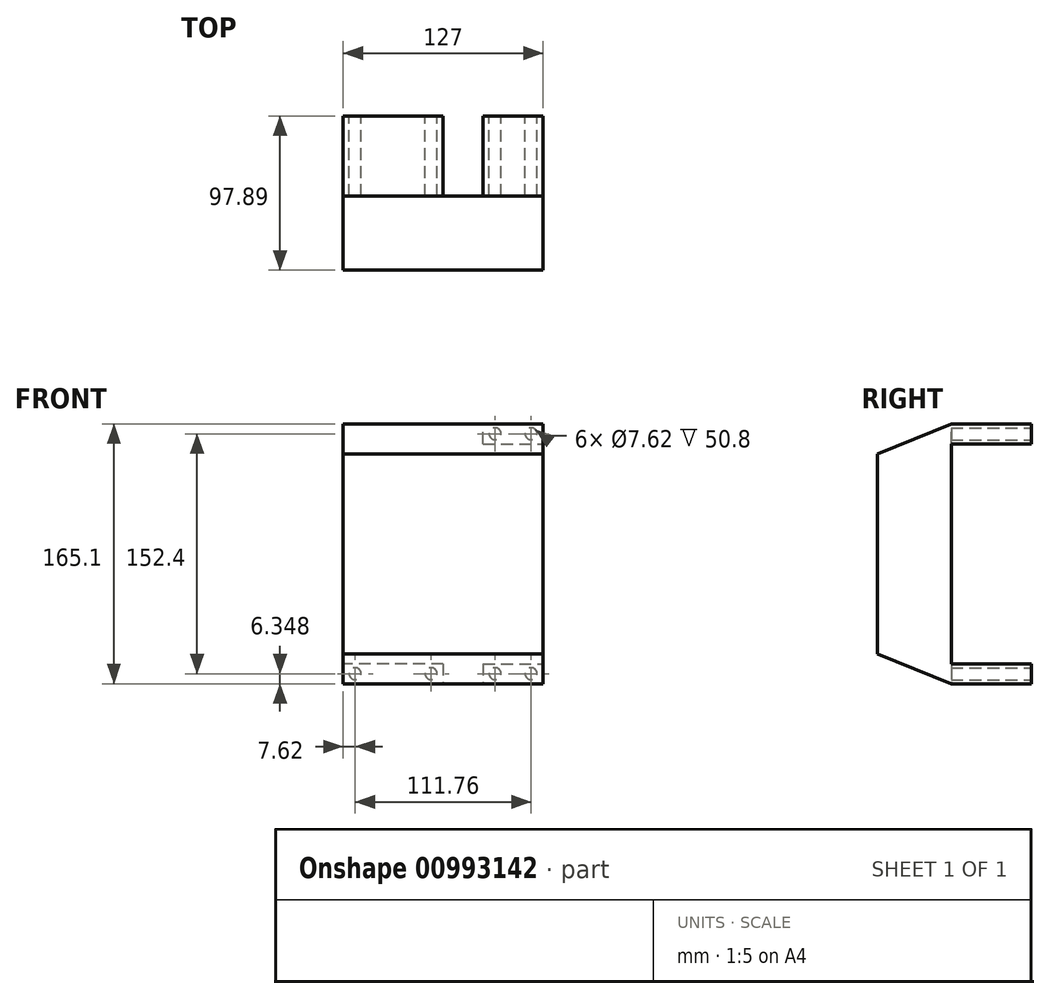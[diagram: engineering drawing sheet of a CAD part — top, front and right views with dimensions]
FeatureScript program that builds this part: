
annotation { "Feature Type Name" : "Feature", "Feature Type Description" : "" }
export const myFeature = defineFeature(function(context is Context, id is Id, definition is map)
    precondition{}
    {
        {
            var Q0;
            Q0=qCreatedBy(makeId("Right.planeOp"),FACE);
            var sketch = newSketch(context, id + "F0", { "sketchPlane" : qUnion([Q0])});
            skLineSegment(sketch, "E0", {"start": v(37.9, 107.88) * mm, "end": v(37.9, -57.22) * mm});
            skLineSegment(sketch, "E1", {"start": v(37.9, 107.88) * mm, "end": v(-9.2, 88.83) * mm});
            skLineSegment(sketch, "E2", {"start": v(-9.2, 88.83) * mm, "end": v(-9.2, -38.17) * mm});
            skLineSegment(sketch, "E3", {"start": v(-9.2, -38.17) * mm, "end": v(37.9, -57.22) * mm});
            skLineSegment(sketch, "E4.bottom", {"start": v(37.9, -57.22) * mm, "end": v(88.7, -57.22) * mm});
            skLineSegment(sketch, "E4.top", {"start": v(37.9, -44.52) * mm, "end": v(88.7, -44.52) * mm});
            skLineSegment(sketch, "E4.left", {"start": v(37.9, -57.22) * mm, "end": v(37.9, -44.52) * mm});
            skLineSegment(sketch, "E4.right", {"start": v(88.7, -57.22) * mm, "end": v(88.7, -44.52) * mm});
            skSolve(sketch);
        }
        {
            var Q0;
            Q0=makeQuery(id+"F0.imprint","IMPRINT",FACE,{"disambiguationData":[TD([[makeQuery(id+"F0.imprint","IMPRINT",EDGE,{"derivedFrom":sQuery(id+"F0.wireOp",EDGE,"E0")}),-1.0]])]});
            extrude(context, id + "F1", {"entities" : qUnion([Q0]), "depth" : 127 * mm, "offsetDistance" : 25.4 * mm});
        }
        {
            var Q0;
            Q0=makeQuery(id+"F0.imprint","IMPRINT",FACE,{"disambiguationData":[TD([[makeQuery(id+"F0.imprint","IMPRINT",EDGE,{"derivedFrom":sQuery(id+"F0.wireOp",EDGE,"E4.bottom")}),1.0]])]});
            extrude(context, id + "F2", {"entities" : qUnion([Q0]), "operationType" : NewBodyOperationType.ADD, "depth" : 63.5 * mm, "offsetDistance" : 25.4 * mm});
        }
        {
            var Q0;
            Q0=makeQuery(id+"F1.opExtrude","SWEPT_FACE",FACE,{"disambiguationData":[OSD([sQuery(id+"F0.wireOp",EDGE,"E0"),sQuery(id+"F0.wireOp",EDGE,"E4.left")])]});
            var sketch = newSketch(context, id + "F3", { "sketchPlane" : qUnion([Q0])});
            skLineSegment(sketch, "E5.bottom", {"start": v(-88.9, -44.52) * mm, "end": v(-127, -44.52) * mm});
            skLineSegment(sketch, "E5.top", {"start": v(-88.9, -57.22) * mm, "end": v(-127, -57.22) * mm});
            skLineSegment(sketch, "E5.left", {"start": v(-88.9, -44.52) * mm, "end": v(-88.9, -57.22) * mm});
            skLineSegment(sketch, "E5.right", {"start": v(-127, -44.52) * mm, "end": v(-127, -57.22) * mm});
            skLineSegment(sketch, "E6.bottom", {"start": v(-88.9, 95.18) * mm, "end": v(-127, 95.18) * mm});
            skLineSegment(sketch, "E6.top", {"start": v(-88.9, 107.88) * mm, "end": v(-127, 107.88) * mm});
            skLineSegment(sketch, "E6.left", {"start": v(-88.9, 95.18) * mm, "end": v(-88.9, 107.88) * mm});
            skLineSegment(sketch, "E6.right", {"start": v(-127, 95.18) * mm, "end": v(-127, 107.88) * mm});
            skSolve(sketch);
        }
        {
            var Q0;
            Q0=makeQuery(id+"F3.imprint","IMPRINT",FACE,{"disambiguationData":[TD([[makeQuery(id+"F3.imprint","IMPRINT",EDGE,{"derivedFrom":sQuery(id+"F3.wireOp",EDGE,"E5.bottom")}),1.0]])]});
            var Q1;
            Q1=makeQuery(id+"F3.imprint","IMPRINT",FACE,{"disambiguationData":[TD([[makeQuery(id+"F3.imprint","IMPRINT",EDGE,{"derivedFrom":sQuery(id+"F3.wireOp",EDGE,"E6.bottom")}),-1.0]])]});
            extrude(context, id + "F4", {"entities" : qUnion([Q0, Q1]), "operationType" : NewBodyOperationType.ADD, "depth" : 50.8 * mm, "offsetDistance" : 25.4 * mm});
        }
        {
            var Q0;
            Q0=makeQuery(id+"F4.opExtrude","CAP_FACE",FACE,{"disambiguationData":[OSD([sQuery(id+"F3.wireOp",EDGE,"E6.bottom"),sQuery(id+"F3.wireOp",EDGE,"E6.top"),sQuery(id+"F3.wireOp",EDGE,"E6.left"),sQuery(id+"F3.wireOp",EDGE,"E6.right")])],"isStart":false});
            var sketch = newSketch(context, id + "F5", { "sketchPlane" : qUnion([Q0])});
            skCircle(sketch, "E7", {"center": v(-96.52, 101.53) * mm, "radius": 3.81 * mm});
            skPoint(sketch, "E7.centerSnap0", {"position": v(-88.9, 101.53) * mm});
            skCircle(sketch, "E8", {"center": v(-119.38, 101.53) * mm, "radius": 3.81 * mm});
            skPoint(sketch, "E8.centerSnap0", {"position": v(-127, 101.53) * mm});
            skSolve(sketch);
        }
        {
            var Q0;
            Q0=makeQuery(id+"F5.imprint","IMPRINT",FACE,{"disambiguationData":[TD([[makeQuery(id+"F5.imprint","IMPRINT",EDGE,{"derivedFrom":sQuery(id+"F5.wireOp",EDGE,"E7")}),1.0]])]});
            var Q1;
            Q1=makeQuery(id+"F5.imprint","IMPRINT",FACE,{"disambiguationData":[TD([[makeQuery(id+"F5.imprint","IMPRINT",EDGE,{"derivedFrom":sQuery(id+"F5.wireOp",EDGE,"E8")}),1.0]])]});
            extrude(context, id + "F6", {"entities" : qUnion([Q0, Q1]), "operationType" : NewBodyOperationType.REMOVE, "oppositeDirection" : true, "depth" : 50.8 * mm, "offsetDistance" : 25.4 * mm});
        }
        {
            var Q0;
            Q0=makeQuery(id+"F4.opExtrude","CAP_FACE",FACE,{"disambiguationData":[OSD([sQuery(id+"F3.wireOp",EDGE,"E5.bottom"),sQuery(id+"F3.wireOp",EDGE,"E5.top"),sQuery(id+"F3.wireOp",EDGE,"E5.left"),sQuery(id+"F3.wireOp",EDGE,"E5.right")])],"isStart":false});
            var sketch = newSketch(context, id + "F7", { "sketchPlane" : qUnion([Q0])});
            skCircle(sketch, "E9", {"center": v(-96.52, -50.87) * mm, "radius": 3.81 * mm});
            skPoint(sketch, "E9.centerSnap0", {"position": v(-88.9, -50.87) * mm});
            skCircle(sketch, "E10", {"center": v(-119.38, -50.87) * mm, "radius": 3.81 * mm});
            skPoint(sketch, "E10.centerSnap0", {"position": v(-127, -50.87) * mm});
            skSolve(sketch);
        }
        {
            var Q0;
            Q0=makeQuery(id+"F7.imprint","IMPRINT",FACE,{"disambiguationData":[TD([[makeQuery(id+"F7.imprint","IMPRINT",EDGE,{"derivedFrom":sQuery(id+"F7.wireOp",EDGE,"E9")}),1.0]])]});
            var Q1;
            Q1=makeQuery(id+"F7.imprint","IMPRINT",FACE,{"disambiguationData":[TD([[makeQuery(id+"F7.imprint","IMPRINT",EDGE,{"derivedFrom":sQuery(id+"F7.wireOp",EDGE,"E10")}),1.0]])]});
            extrude(context, id + "F8", {"entities" : qUnion([Q0, Q1]), "operationType" : NewBodyOperationType.REMOVE, "oppositeDirection" : true, "depth" : 50.8 * mm, "offsetDistance" : 25.4 * mm});
        }
        {
            var Q0;
            Q0=makeQuery(id+"F2.opExtrude","SWEPT_FACE",FACE,{"disambiguationData":[OSD([sQuery(id+"F0.wireOp",EDGE,"E4.right")])]});
            var sketch = newSketch(context, id + "F9", { "sketchPlane" : qUnion([Q0])});
            skCircle(sketch, "E11", {"center": v(-55.88, -50.87) * mm, "radius": 3.81 * mm});
            skPoint(sketch, "E11.centerSnap0", {"position": v(-63.5, -50.87) * mm});
            skCircle(sketch, "E12", {"center": v(-7.62, -50.87) * mm, "radius": 3.81 * mm});
            skSolve(sketch);
        }
        {
            var Q0;
            Q0=makeQuery(id+"F9.imprint","IMPRINT",FACE,{"disambiguationData":[TD([[makeQuery(id+"F9.imprint","IMPRINT",EDGE,{"derivedFrom":sQuery(id+"F9.wireOp",EDGE,"E11")}),1.0]])]});
            var Q1;
            Q1=makeQuery(id+"F9.imprint","IMPRINT",FACE,{"disambiguationData":[TD([[makeQuery(id+"F9.imprint","IMPRINT",EDGE,{"derivedFrom":sQuery(id+"F9.wireOp",EDGE,"E12")}),1.0]])]});
            extrude(context, id + "F10", {"entities" : qUnion([Q0, Q1]), "operationType" : NewBodyOperationType.REMOVE, "oppositeDirection" : true, "depth" : 50.8 * mm, "offsetDistance" : 25.4 * mm});
        }
    });
